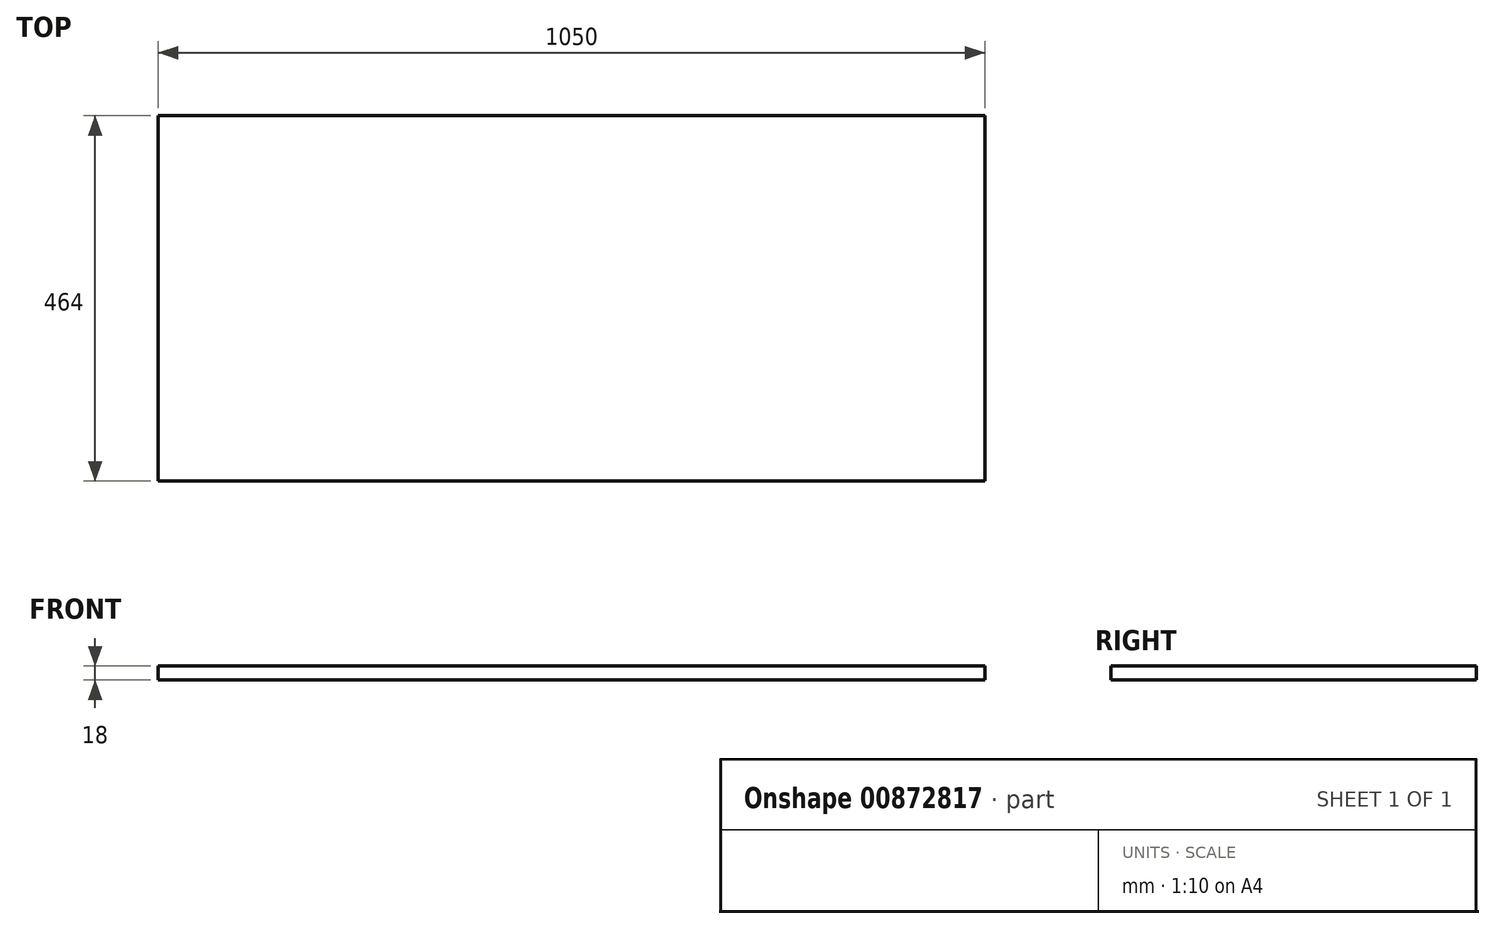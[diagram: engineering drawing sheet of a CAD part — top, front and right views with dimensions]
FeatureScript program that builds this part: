
annotation { "Feature Type Name" : "Feature", "Feature Type Description" : "" }
export const myFeature = defineFeature(function(context is Context, id is Id, definition is map)
    precondition{}
    {
        {
            var Q0;
            Q0=qCreatedBy(makeId("Top.planeOp"),FACE);
            var sketch = newSketch(context, id + "F0", { "sketchPlane" : qUnion([Q0])});
            skLineSegment(sketch, "E0.bottom", {"start": v(525, -232) * mm, "end": v(-525, -232) * mm});
            skLineSegment(sketch, "E0.top", {"start": v(525, 232) * mm, "end": v(-525, 232) * mm});
            skLineSegment(sketch, "E0.left", {"start": v(525, -232) * mm, "end": v(525, 232) * mm});
            skLineSegment(sketch, "E0.right", {"start": v(-525, -232) * mm, "end": v(-525, 232) * mm});
            skPoint(sketch, "E0.middle", {"position": v(0, 0) * mm});
            skSolve(sketch);
        }
        {
            var Q0;
            Q0 = qSketchRegion(id + "F0", true);
            extrude(context, id + "F1", {"entities" : qUnion([Q0]), "depth" : 18 * mm, "offsetDistance" : 25 * mm});
        }
    });
